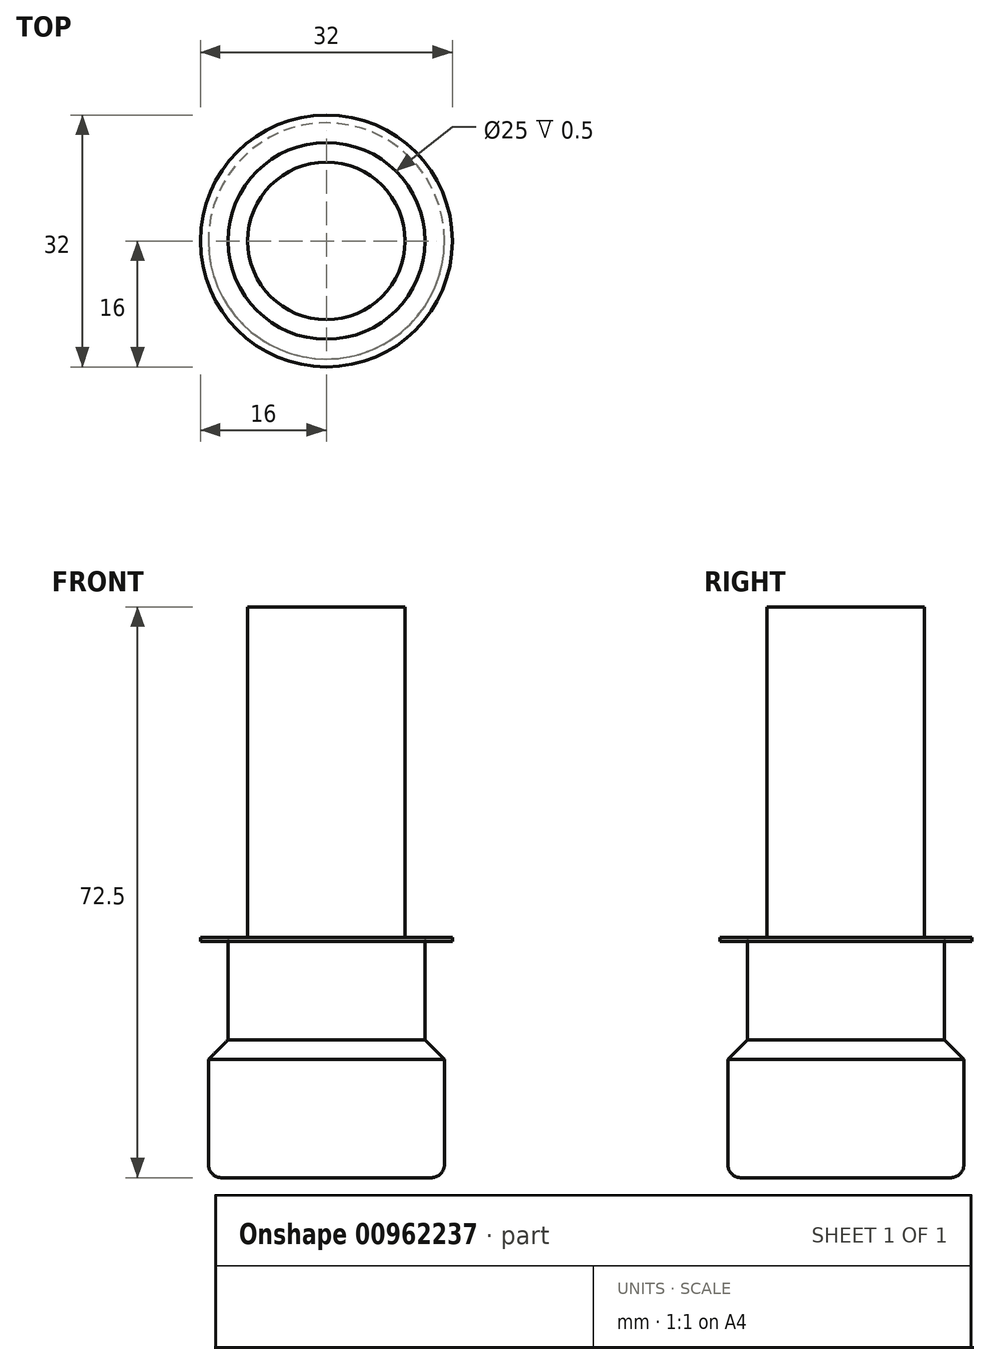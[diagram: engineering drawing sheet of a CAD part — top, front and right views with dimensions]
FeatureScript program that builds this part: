
annotation { "Feature Type Name" : "Feature", "Feature Type Description" : "" }
export const myFeature = defineFeature(function(context is Context, id is Id, definition is map)
    precondition{}
    {
        {
            var Q0;
            Q0=qCreatedBy(makeId("Top.planeOp"),FACE);
            var sketch = newSketch(context, id + "F0", { "sketchPlane" : qUnion([Q0])});
            skCircle(sketch, "E0", {"center": v(0, 0) * mm, "radius": 15 * mm});
            skSolve(sketch);
        }
        {
            var Q0;
            Q0=makeQuery(id+"F0.imprint","IMPRINT",FACE,{"disambiguationData":[TD([[makeQuery(id+"F0.imprint","IMPRINT",EDGE,{"derivedFrom":sQuery(id+"F0.wireOp",EDGE,"E0")}),1.0]])]});
            extrude(context, id + "F1", {"entities" : qUnion([Q0]), "depth" : 20 * mm, "offsetDistance" : 25 * mm});
        }
        {
            var Q0;
            Q0=makeQuery(id+"F1.opExtrude","CAP_FACE",FACE,{"disambiguationData":[OSD([sQuery(id+"F0.wireOp",EDGE,"E0")])],"isStart":false});
            var sketch = newSketch(context, id + "F2", { "sketchPlane" : qUnion([Q0])});
            skCircle(sketch, "E1", {"center": v(0, 0) * mm, "radius": 12.5 * mm});
            skSolve(sketch);
        }
        {
            var Q0;
            Q0=makeQuery(id+"F2.imprint","IMPRINT",FACE,{"disambiguationData":[TD([[makeQuery(id+"F2.imprint","IMPRINT",EDGE,{"derivedFrom":sQuery(id+"F2.wireOp",EDGE,"E1")}),1.0]])]});
            extrude(context, id + "F3", {"entities" : qUnion([Q0]), "operationType" : NewBodyOperationType.ADD, "depth" : 10 * mm, "offsetDistance" : 25 * mm});
        }
        {
            var Q0;
            Q0=makeQuery(id+"F3.opExtrude","CAP_FACE",FACE,{"disambiguationData":[OSD([sQuery(id+"F2.wireOp",EDGE,"E1")])],"isStart":false});
            var sketch = newSketch(context, id + "F4", { "sketchPlane" : qUnion([Q0])});
            skCircle(sketch, "E2", {"center": v(0, 0) * mm, "radius": 16 * mm});
            skSolve(sketch);
        }
        {
            var Q0;
            Q0=makeQuery(id+"F4.imprint","IMPRINT",FACE,{"disambiguationData":[TD([[makeQuery(id+"F4.imprint","IMPRINT",EDGE,{"derivedFrom":sQuery(id+"F4.wireOp",EDGE,"E2")}),1.0]])]});
            extrude(context, id + "F5", {"entities" : qUnion([Q0]), "depth" : 0.5 * mm, "offsetDistance" : 25 * mm});
        }
        {
            var Q0;
            Q0=makeQuery(id+"F5.opExtrude","CAP_FACE",FACE,{"disambiguationData":[OSD([sQuery(id+"F2.wireOp",EDGE,"E1"),sQuery(id+"F4.wireOp",EDGE,"E2")])],"isStart":false});
            var sketch = newSketch(context, id + "F6", { "sketchPlane" : qUnion([Q0])});
            skCircle(sketch, "E3", {"center": v(0, 0) * mm, "radius": 10 * mm});
            skSolve(sketch);
        }
        {
            var Q0;
            Q0=makeQuery(id+"F6.imprint","IMPRINT",FACE,{"disambiguationData":[TD([[makeQuery(id+"F6.imprint","IMPRINT",EDGE,{"derivedFrom":sQuery(id+"F6.wireOp",EDGE,"E3")}),1.0]])]});
            extrude(context, id + "F7", {"entities" : qUnion([Q0]), "depth" : 42 * mm, "offsetDistance" : 25 * mm});
        }
        {
            var Q0;
            Q0=makeQuery(id+"F1.opExtrude","CAP_EDGE",EDGE,{"disambiguationData":[OSD([sQuery(id+"F0.wireOp",EDGE,"E0")])],"isStart":true});
            fillet(context, id + "F8", {"entities" : qUnion([Q0]), "radius" : 1.69 * mm, "tangentPropagation" : true, "allowEdgeOverflow" : false});
        }
        {
            var Q0;
            Q0=makeQuery(id+"F1.opExtrude","CAP_EDGE",EDGE,{"disambiguationData":[OSD([sQuery(id+"F0.wireOp",EDGE,"E0")])],"isStart":false});
            chamfer(context, id + "F9", {"entities" : qUnion([Q0]), "width" : 5 * mm, "tangentPropagation" : true});
        }
    });
